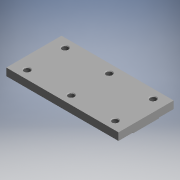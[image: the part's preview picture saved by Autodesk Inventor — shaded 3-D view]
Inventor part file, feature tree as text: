
AUTODESK INVENTOR PART (.ipt)
format: ipt  version: 2017.3 (Build 213256000, 256)  size: 248,832 bytes
history: native  units: mm (DEFAULTED — no unit token found)
features: other x7, sketch x5, extrude x4, revolve x1, thread x1, pattern_linear x1
ambient origin geometry x8: Origin, YZ Plane, XZ Plane, XY Plane, X Axis, Y Axis, Z Axis, Center Point
bodies: Solid1 (feature_tree)
feature tree (19):
  extrude  "Extrusion1"  Depth=65.0mm TaperAngle=0.0deg
  extrude  "Extrusion2"  TaperAngle=360.0deg  [1 undecoded]
  extrude  "Extrusion3"  Depth=30.0mm
  revolve  "Revolution1"  [1 undecoded]
  thread  "Thread1"  [1 undecoded]
  pattern_linear  "Rectangular Pattern1"  [2 undecoded]
  extrude  "Extrusion4"  [1 undecoded]
  other  "tbck_XY"
  other  "tbck_YZ"
  other  "tbck_ZX"
  other  "tbck_X"
  other  "tbck_Y"
  other  "tbck_Z"
  other  "tbck_Center"
  sketch  "Sketch_1"  dims[d0=6.0mm d1=0.0mm d2=65.0mm d3=0.0mm]
  sketch  "Sketch_2"  dims[d4=65.0mm d5=0.0mm d6=360.0deg]
  sketch  "Sketch_3"  dims[d7=3.542mm d8=0.0mm d9=30.0mm d11=25.5mm d12=20.0mm d14=22.0mm]
  sketch  "Sketch_4"  dims[d15=15.0mm d16=0.0mm]
  sketch  "Sketch_8"
note: 6 required parameter values undecoded (feature->parameter linkage not recoverable at this tier; creation-order binding heuristic only, values carry confidence <= 0.55)
